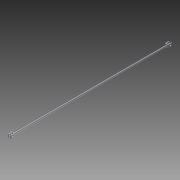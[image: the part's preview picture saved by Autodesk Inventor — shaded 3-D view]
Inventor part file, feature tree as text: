
AUTODESK INVENTOR PART (.ipt)
format: ipt  version: 2012 (Build 160160000, 160)  size: 129,024 bytes
history: native  units: in
note: dims shown in document units (in); Inventor stores cm internally (conversion verified against a paired STEP export)
features: extrude x3, sketch x3, projected_geometry x2, fillet x1
ambient origin geometry x8: Origin, YZ Plane, XZ Plane, XY Plane, X Axis, Y Axis, Z Axis, Center Point
bodies: Solid1 (feature_tree)
feature tree (9):
  extrude  "Extrusion1"  Depth=0.5in
  extrude  "Extrusion2"  Depth=0.625in
  extrude  "Extrusion3"  Depth=0.625in
  fillet  "Fillet1"  Radius=0.5in
  sketch  "Sketch1"  dims[d0=0.5in d1=0.5in]
  sketch  "Sketch2"  dims[d2=25.5312in d3=0.0in d4=0.625in]
  sketch  "Sketch3"  dims[d5=0.25in d6=0.625in d7=0.5in d8=0.5in d9=25.0in d10=0.0in d11=0.25in d12=0.25in d13=0.25in d14=0.25in d15=0.125in d16=0.25in d17=0.25in d18=0.25in d19=25.0in d20=0.0in d21=0.125in]
  projected_geometry  "Projected Loop1"
  projected_geometry  "Projected Loop2"
